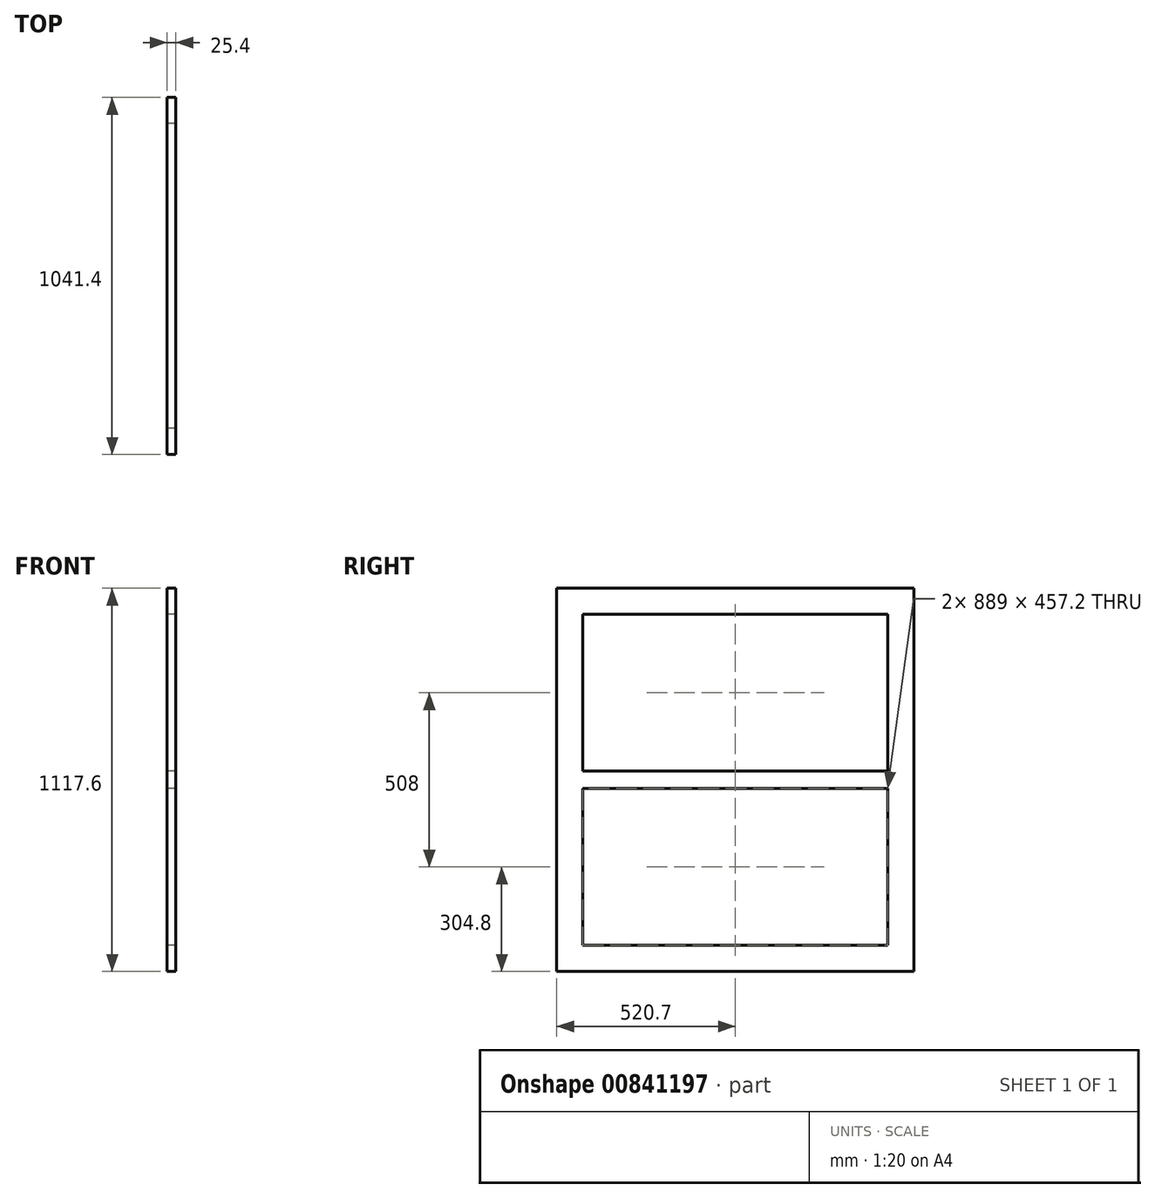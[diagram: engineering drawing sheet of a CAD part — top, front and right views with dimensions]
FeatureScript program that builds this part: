
annotation { "Feature Type Name" : "Feature", "Feature Type Description" : "" }
export const myFeature = defineFeature(function(context is Context, id is Id, definition is map)
    precondition{}
    {
        {
            var Q0;
            Q0=qCreatedBy(makeId("Right.planeOp"),FACE);
            var sketch = newSketch(context, id + "F0", { "sketchPlane" : qUnion([Q0])});
            skLineSegment(sketch, "E0.bottom", {"start": v(0, 1117.6) * mm, "end": v(1041.4, 1117.6) * mm});
            skLineSegment(sketch, "E0.top", {"start": v(0, 0) * mm, "end": v(1041.4, 0) * mm});
            skLineSegment(sketch, "E0.left", {"start": v(0, 1117.6) * mm, "end": v(0, 0) * mm});
            skLineSegment(sketch, "E0.right", {"start": v(1041.4, 1117.6) * mm, "end": v(1041.4, 0) * mm});
            skLineSegment(sketch, "E1.bottom", {"start": v(76.2, 1041.4) * mm, "end": v(965.2, 1041.4) * mm});
            skLineSegment(sketch, "E1.top", {"start": v(76.2, 76.2) * mm, "end": v(965.2, 76.2) * mm});
            skLineSegment(sketch, "E1.left", {"start": v(76.2, 1041.4) * mm, "end": v(76.2, 584.2) * mm});
            skLineSegment(sketch, "E1.right", {"start": v(965.2, 1041.4) * mm, "end": v(965.2, 584.2) * mm});
            skLineSegment(sketch, "E2", {"start": v(76.2, 584.2) * mm, "end": v(965.2, 584.2) * mm});
            skLineSegment(sketch, "E3", {"start": v(965.2, 533.4) * mm, "end": v(76.2, 533.4) * mm});
            skLineSegment(sketch, "E4.trimOffspring", {"start": v(76.2, 533.4) * mm, "end": v(76.2, 76.2) * mm});
            skLineSegment(sketch, "E5.trimOffspring", {"start": v(965.2, 533.4) * mm, "end": v(965.2, 76.2) * mm});
            skSolve(sketch);
        }
        {
            var Q0;
            Q0=makeQuery(id+"F0.imprint","IMPRINT",FACE,{"disambiguationData":[TD([[makeQuery(id+"F0.imprint","IMPRINT",EDGE,{"derivedFrom":sQuery(id+"F0.wireOp",EDGE,"E0.bottom")}),-1.0]])]});
            extrude(context, id + "F1", {"entities" : qUnion([Q0]), "depth" : 25.4 * mm, "offsetDistance" : 25.4 * mm});
        }
    });
